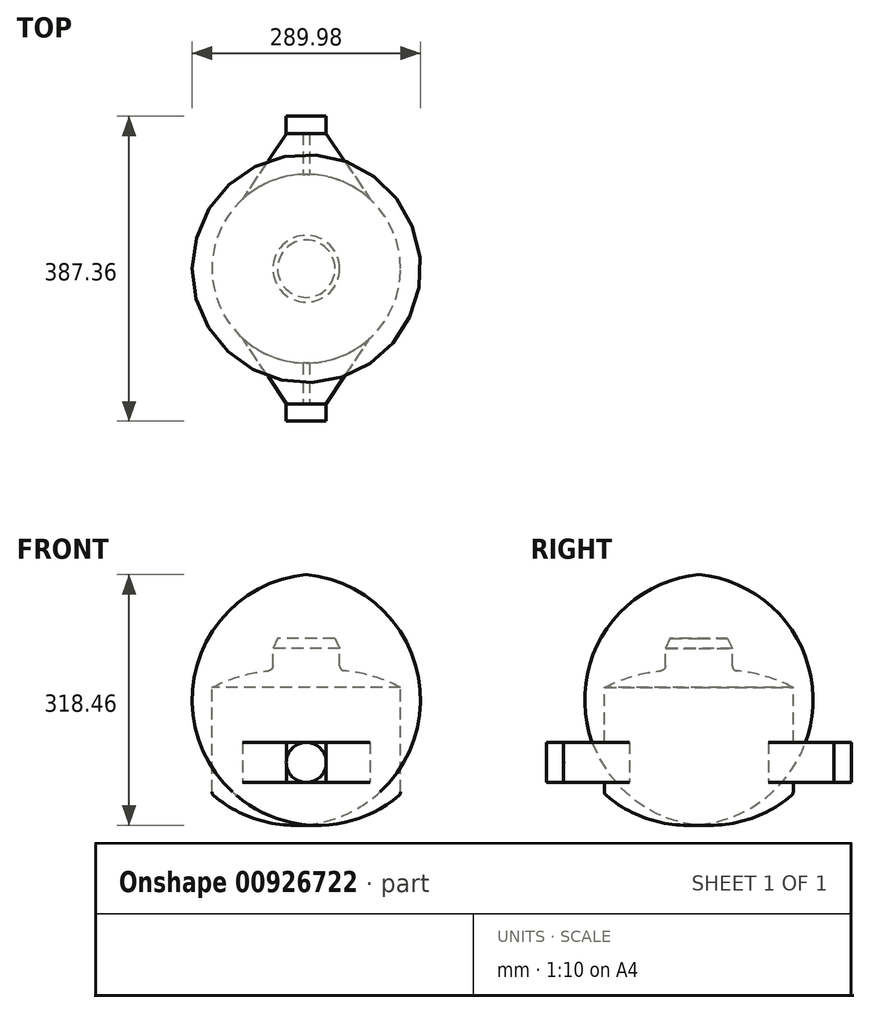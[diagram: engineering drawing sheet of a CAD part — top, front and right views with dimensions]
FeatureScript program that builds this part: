
annotation { "Feature Type Name" : "Feature", "Feature Type Description" : "" }
export const myFeature = defineFeature(function(context is Context, id is Id, definition is map)
    precondition{}
    {
        {
            var Q0;
            Q0=qCreatedBy(makeId("Right.planeOp"),FACE);
            var sketch = newSketch(context, id + "F0", { "sketchPlane" : qUnion([Q0])});
            skLineSegment(sketch, "E0", {"start": v(0, 118.27) * mm, "end": v(0, -118.27) * mm, "construction": true});
            skLineSegment(sketch, "E1", {"start": v(0, 118.27) * mm, "end": v(-36.44, 118.27) * mm});
            skLineSegment(sketch, "E2", {"start": v(-42.48, 105.81) * mm, "end": v(-36.44, 118.27) * mm});
            skLineSegment(sketch, "E3", {"start": v(-42.48, 105.81) * mm, "end": v(-42.48, 83.7) * mm});
            skLineSegment(sketch, "E4", {"start": v(-119.86, -76.36) * mm, "end": v(-119.86, 56.1) * mm});
            skArc(sketch, "E5", {"start": v(-48.2, 77.38) * mm, "mid": v(-85.02, 70.11) * mm, "end": v(-119.86, 56.1) * mm});
            skPoint(sketch, "E6.visualSharp", {"position": v(-42.48, 77.88) * mm});
            skArc(sketch, "E6.filletArc", {"start": v(-48.2, 77.38) * mm, "mid": v(-44.12, 79.44) * mm, "end": v(-42.48, 83.7) * mm});
            skArc(sketch, "E7", {"start": v(-117.6, -81.21) * mm, "mid": v(-62.53, -111.56) * mm, "end": v(0, -118.27) * mm});
            skPoint(sketch, "E8.visualSharp", {"position": v(-119.86, -79.27) * mm});
            skArc(sketch, "E8.filletArc", {"start": v(-119.86, -76.36) * mm, "mid": v(-119.27, -79.04) * mm, "end": v(-117.6, -81.21) * mm});
            skLineSegment(sketch, "E9", {"start": v(0, 118.27) * mm, "end": v(0, -118.27) * mm});
            skSolve(sketch);
        }
        {
            var Q0;
            Q0 = qSketchRegion(id + "F0", true);
            var Q1;
            Q1=sQuery(id+"F0.wireOp",EDGE,"E9");
            revolve(context, id + "F1", {"surfaceOperationType" : NewSurfaceOperationType.NEW, "entities" : qUnion([Q0]), "axis" : qUnion([Q1]), "revolveType" : RevolveType.FULL});
        }
        {
            var Q0;
            Q0=qCreatedBy(makeId("Right.planeOp"),FACE);
            var sketch = newSketch(context, id + "F2", { "sketchPlane" : qUnion([Q0])});
            skLineSegment(sketch, "E10", {"start": v(-193.67, -39.24) * mm, "end": v(193.68, -39.24) * mm, "construction": true});
            skLineSegment(sketch, "E11", {"start": v(-193.67, -39.24) * mm, "end": v(-193.67, -13.84) * mm});
            skLineSegment(sketch, "E12", {"start": v(-193.67, -13.84) * mm, "end": v(193.68, -13.84) * mm});
            skLineSegment(sketch, "E13", {"start": v(193.68, -13.84) * mm, "end": v(193.68, -39.24) * mm});
            skLineSegment(sketch, "E14", {"start": v(-193.67, -39.24) * mm, "end": v(193.68, -39.24) * mm});
            skSolve(sketch);
        }
        {
            var Q0;
            Q0 = qSketchRegion(id + "F2", true);
            var Q1;
            Q1=sQuery(id+"F2.wireOp",EDGE,"E14");
            revolve(context, id + "F3", {"operationType" : NewBodyOperationType.ADD, "surfaceOperationType" : NewSurfaceOperationType.NEW, "entities" : qUnion([Q0]), "axis" : qUnion([Q1]), "revolveType" : RevolveType.FULL});
        }
        {
            var Q0;
            Q0=qCreatedBy(makeId("Top.planeOp"),FACE);
            cPlane(context, id + "F4", {"entities" : qUnion([Q0]), "cplaneType" : CPlaneType.OFFSET, "offset" : 38.9 * mm, "oppositeDirection" : true, "width" : 152.4 * mm, "height" : 152.4 * mm});
        }
        {
            var Q0;
            Q0=qCreatedBy(id+"F4.planeOp",FACE);
            var sketch = newSketch(context, id + "F5", { "sketchPlane" : qUnion([Q0])});
            skLineSegment(sketch, "E15", {"start": v(0, 193.92) * mm, "end": v(0, -195.58) * mm, "construction": true});
            skLineSegment(sketch, "E16", {"start": v(0, 171.73) * mm, "end": v(-25.34, 171.73) * mm});
            skArc(sketch, "E17.0", {"start": v(-81.01, 88.33) * mm, "mid": v(-119.86, 0) * mm, "end": v(-81.01, -88.33) * mm});
            skLineSegment(sketch, "E18", {"start": v(-25.34, 171.73) * mm, "end": v(-81.01, 88.33) * mm});
            skLineSegment(sketch, "E19", {"start": v(0, 0) * mm, "end": v(-186.63, 0) * mm, "construction": true});
            skLineSegment(sketch, "E20.MirrorCS", {"start": v(-25.34, -171.73) * mm, "end": v(-81.01, -88.33) * mm});
            skLineSegment(sketch, "E21.MirrorCS", {"start": v(0, -171.73) * mm, "end": v(-25.34, -171.73) * mm});
            skLineSegment(sketch, "E22.MirrorCS", {"start": v(0, 171.73) * mm, "end": v(25.34, 171.73) * mm});
            skLineSegment(sketch, "E23.MirrorCS", {"start": v(25.34, -171.73) * mm, "end": v(81.01, -88.33) * mm});
            skArc(sketch, "E24.MirrorCS", {"start": v(81.01, 88.33) * mm, "mid": v(119.86, 0) * mm, "end": v(81.01, -88.33) * mm});
            skLineSegment(sketch, "E25.MirrorCS", {"start": v(0, -171.73) * mm, "end": v(25.34, -171.73) * mm});
            skLineSegment(sketch, "E26.MirrorCS", {"start": v(25.34, 171.73) * mm, "end": v(81.01, 88.33) * mm});
            skSolve(sketch);
        }
        {
            var Q0;
            Q0 = qSketchRegion(id + "F5", true);
            extrude(context, id + "F6", {"entities" : qUnion([Q0]), "operationType" : NewBodyOperationType.ADD, "depth" : 50.8 * mm, "offsetDistance" : 25.4 * mm, "symmetric" : true});
        }
    });
